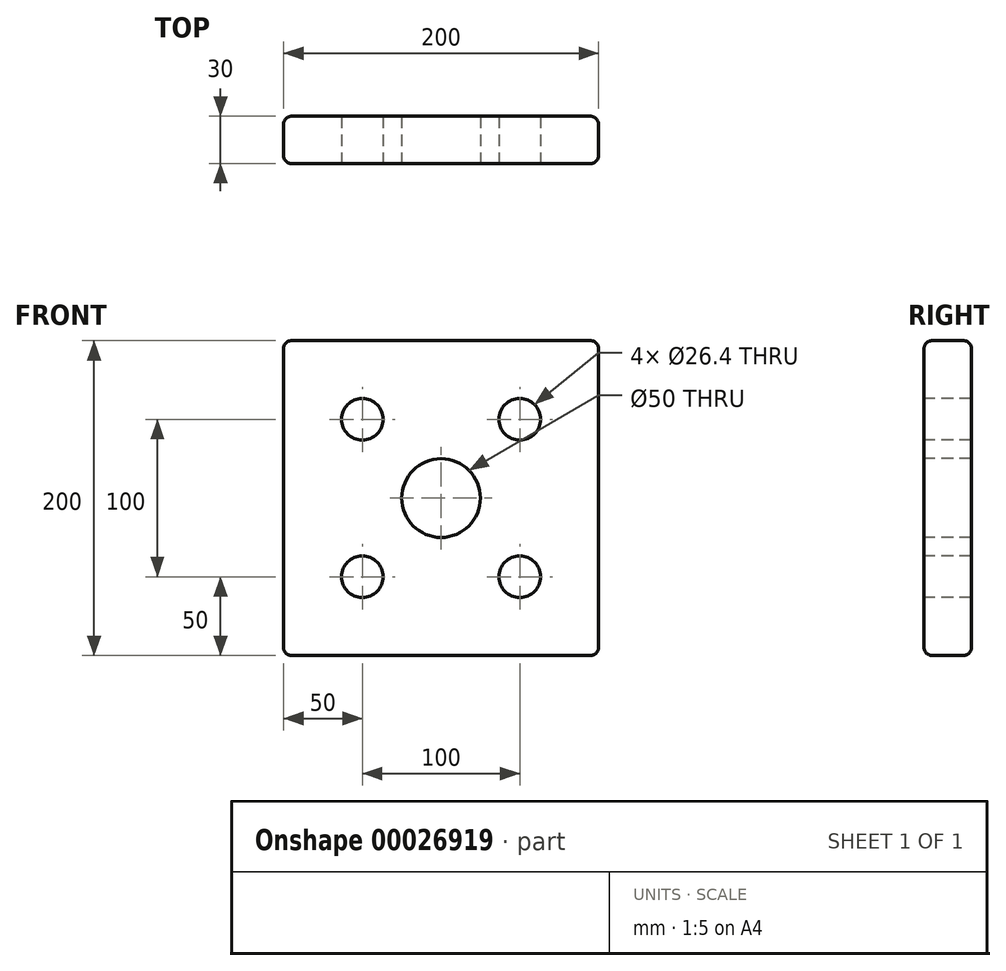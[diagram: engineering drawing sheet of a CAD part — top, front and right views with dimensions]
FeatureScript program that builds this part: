
annotation { "Feature Type Name" : "Feature", "Feature Type Description" : "" }
export const myFeature = defineFeature(function(context is Context, id is Id, definition is map)
    precondition{}
    {
        {
            var Q0;
            Q0=qCreatedBy(makeId("Front.planeOp"),FACE);
            var sketch = newSketch(context, id + "F0", { "sketchPlane" : qUnion([Q0])});
            skLineSegment(sketch, "E0.bottom", {"start": v(-100, 100) * mm, "end": v(100, 100) * mm});
            skLineSegment(sketch, "E0.top", {"start": v(-100, -100) * mm, "end": v(100, -100) * mm});
            skLineSegment(sketch, "E0.left", {"start": v(-100, 100) * mm, "end": v(-100, -100) * mm});
            skLineSegment(sketch, "E0.right", {"start": v(100, 100) * mm, "end": v(100, -100) * mm});
            skSolve(sketch);
        }
        {
            var Q0;
            Q0=qSketchRegion(id+"F0",true);
            extrude(context, id + "F1", {"entities" : qUnion([Q0]), "depth" : 30 * mm});
        }
        {
            var Q0;
            Q0=makeQuery(id+"F1.opExtrude","CAP_FACE",FACE,{"disambiguationData":[OSD([sQuery(id+"F0.wireOp",EDGE,"E0.bottom"),sQuery(id+"F0.wireOp",EDGE,"E0.top"),sQuery(id+"F0.wireOp",EDGE,"E0.left"),sQuery(id+"F0.wireOp",EDGE,"E0.right")])],"isStart":false});
            var sketch = newSketch(context, id + "F2", { "sketchPlane" : qUnion([Q0])});
            skCircle(sketch, "E1", {"center": v(0, 0) * mm, "radius": 25 * mm});
            skSolve(sketch);
        }
        {
            var Q0;
            Q0=makeQuery(id+"F1.opExtrude","CAP_FACE",FACE,{"disambiguationData":[OSD([sQuery(id+"F0.wireOp",EDGE,"E0.bottom"),sQuery(id+"F0.wireOp",EDGE,"E0.top"),sQuery(id+"F0.wireOp",EDGE,"E0.left"),sQuery(id+"F0.wireOp",EDGE,"E0.right")])],"isStart":false});
            var sketch = newSketch(context, id + "F3", { "sketchPlane" : qUnion([Q0])});
            skCircle(sketch, "E2", {"center": v(-50, -50) * mm, "radius": 13.2 * mm});
            skCircle(sketch, "E3.0.1.0", {"center": v(-50, 50) * mm, "radius": 13.2 * mm});
            skCircle(sketch, "E3.1.0.0", {"center": v(50, -50) * mm, "radius": 13.2 * mm});
            skCircle(sketch, "E3.1.1.0", {"center": v(50, 50) * mm, "radius": 13.2 * mm});
            skLineSegment(sketch, "E3.direction1", {"start": v(-50, -50) * mm, "end": v(50, -50) * mm, "construction": true});
            skLineSegment(sketch, "E3.direction2", {"start": v(-50, -50) * mm, "end": v(-50, 50) * mm, "construction": true});
            skLineSegment(sketch, "E4", {"start": v(-66.92, 0) * mm, "end": v(60.8, 0) * mm});
            skLineSegment(sketch, "E5", {"start": v(0, -49.75) * mm, "end": v(0, 68.34) * mm});
            skSolve(sketch);
        }
        {
            var Q0;
            Q0=makeQuery(id+"F1.opExtrude","SWEPT_FACE",FACE,{"disambiguationData":[OSD([sQuery(id+"F0.wireOp",EDGE,"E0.right")])]});
            var Q1;
            Q1=makeQuery(id+"F1.opExtrude","SWEPT_FACE",FACE,{"disambiguationData":[OSD([sQuery(id+"F0.wireOp",EDGE,"E0.top")])]});
            var Q2;
            Q2=makeQuery(id+"F1.opExtrude","CAP_EDGE",EDGE,{"disambiguationData":[OSD([sQuery(id+"F0.wireOp",EDGE,"E0.top")])],"isStart":true});
            var Q3;
            Q3=makeQuery(id+"F1.opExtrude","SWEPT_FACE",FACE,{"disambiguationData":[OSD([sQuery(id+"F0.wireOp",EDGE,"E0.left")])]});
            var Q4;
            Q4=makeQuery(id+"F1.opExtrude","SWEPT_FACE",FACE,{"disambiguationData":[OSD([sQuery(id+"F0.wireOp",EDGE,"E0.bottom")])]});
            fillet(context, id + "F4", {"entities" : qUnion([Q0, Q1, Q2, Q3, Q4]), "radius" : 5 * mm, "tangentPropagation" : true, "allowEdgeOverflow" : false});
        }
        {
            var Q0;
            Q0=qSketchRegion(id+"F2",true);
            extrude(context, id + "F5", {"entities" : qUnion([Q0]), "operationType" : NewBodyOperationType.REMOVE, "endBound" : BoundingType.THROUGH_ALL, "oppositeDirection" : true, "depth" : 25 * mm});
        }
        {
            var Q0;
            Q0=qSketchRegion(id+"F3",true);
            extrude(context, id + "F6", {"entities" : qUnion([Q0]), "operationType" : NewBodyOperationType.REMOVE, "endBound" : BoundingType.THROUGH_ALL, "oppositeDirection" : true, "depth" : 25 * mm});
        }
    });
